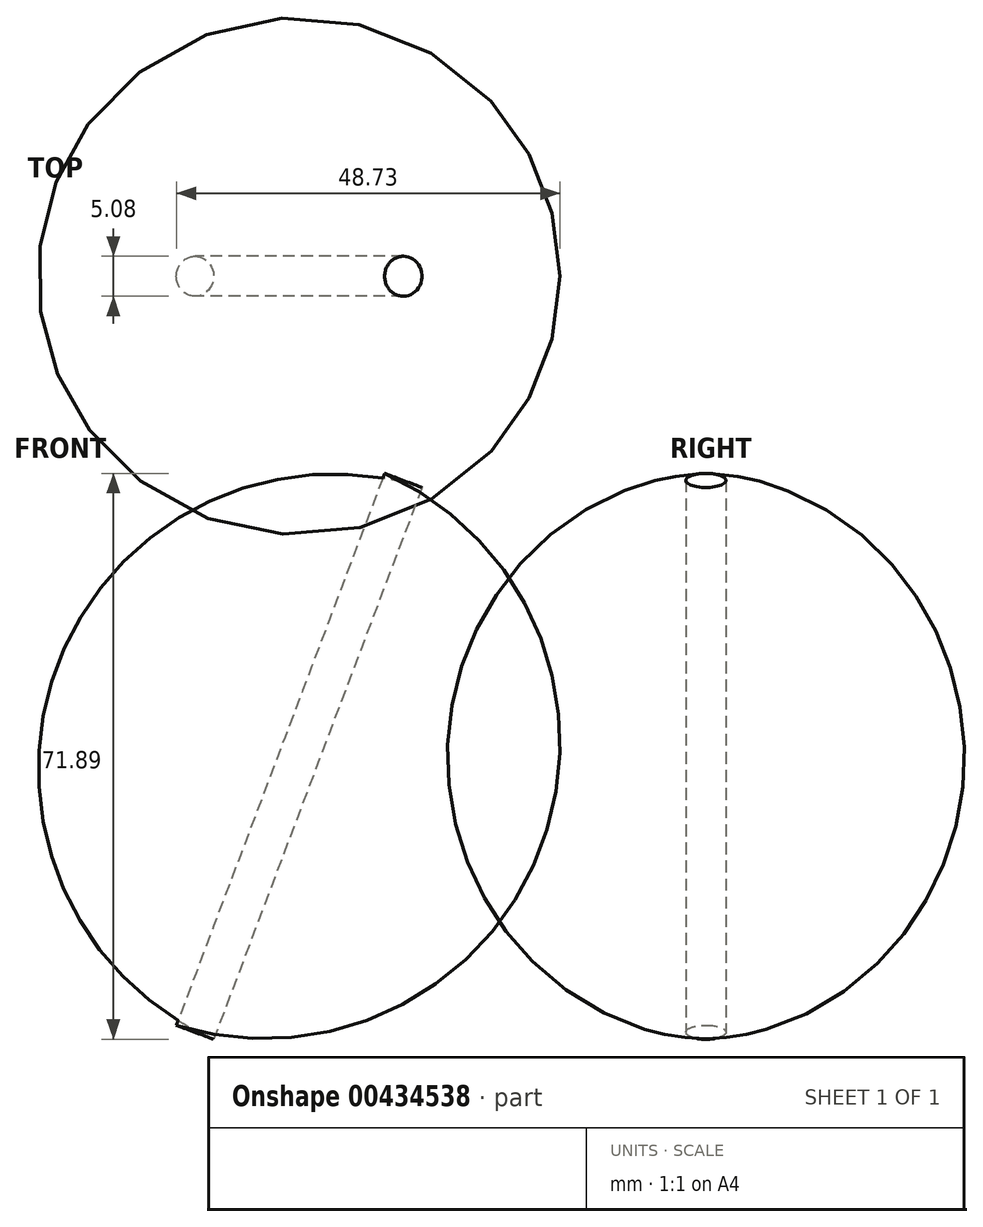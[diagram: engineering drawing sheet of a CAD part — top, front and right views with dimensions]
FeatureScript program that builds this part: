
annotation { "Feature Type Name" : "Feature", "Feature Type Description" : "" }
export const myFeature = defineFeature(function(context is Context, id is Id, definition is map)
    precondition{}
    {
        {
            var Q0;
            Q0=qCreatedBy(makeId("Front.planeOp"),FACE);
            var sketch = newSketch(context, id + "F0", { "sketchPlane" : qUnion([Q0])});
            skLineSegment(sketch, "E0", {"start": v(-26.18, -27.6) * mm, "end": v(0.28, 42.5) * mm});
            skArc(sketch, "E1", {"start": v(-26.18, -27.6) * mm, "mid": v(24.18, -6.56) * mm, "end": v(0.28, 42.5) * mm});
            skLineSegment(sketch, "E2", {"start": v(-28.5, -26.54) * mm, "end": v(-2.03, 43.57) * mm, "construction": true});
            skSolve(sketch);
        }
        {
            var Q0;
            Q0=makeQuery(id+"F0.imprint","IMPRINT",FACE,{"disambiguationData":[TD([[makeQuery(id+"F0.imprint","IMPRINT",EDGE,{"derivedFrom":sQuery(id+"F0.wireOp",EDGE,"E0")}),-1.0]])]});
            var Q1;
            Q1=sQuery(id+"F0.wireOp",EDGE,"E2");
            revolve(context, id + "F1", {"entities" : qUnion([Q0]), "axis" : qUnion([Q1]), "revolveType" : RevolveType.FULL});
        }
    });
